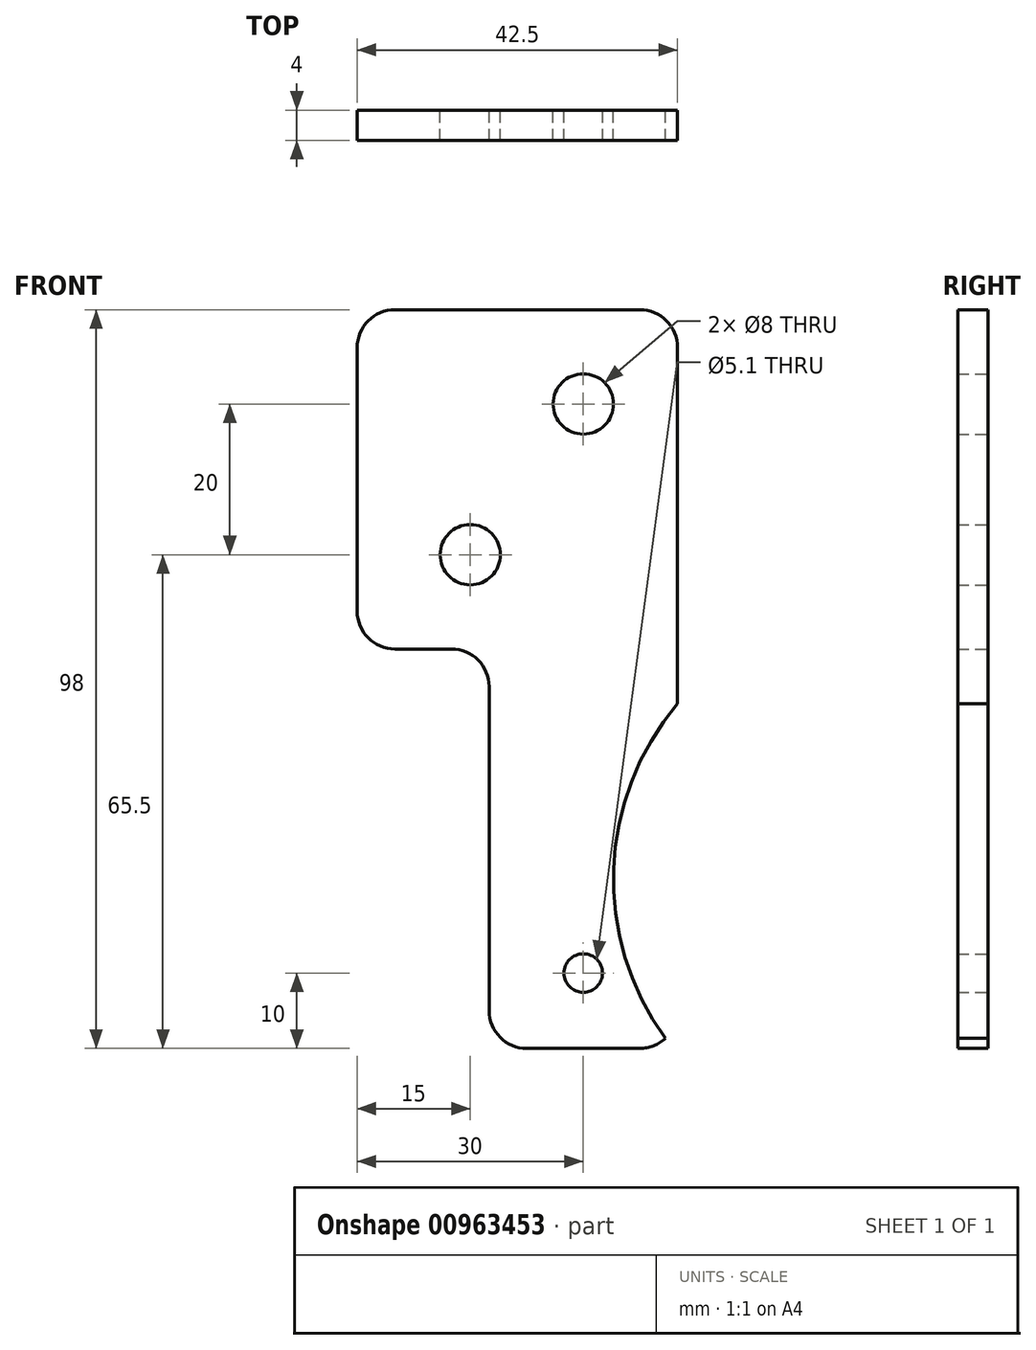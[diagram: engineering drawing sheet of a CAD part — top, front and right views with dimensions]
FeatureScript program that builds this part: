
annotation { "Feature Type Name" : "Feature", "Feature Type Description" : "" }
export const myFeature = defineFeature(function(context is Context, id is Id, definition is map)
    precondition{}
    {
        {
            var Q0;
            Q0=qCreatedBy(makeId("Front.planeOp"),FACE);
            var sketch = newSketch(context, id + "F0", { "sketchPlane" : qUnion([Q0])});
            skLineSegment(sketch, "E0", {"start": v(0, 5) * mm, "end": v(0, 48) * mm});
            skLineSegment(sketch, "E1", {"start": v(-5, 53) * mm, "end": v(-12.5, 53) * mm});
            skLineSegment(sketch, "E2", {"start": v(-17.5, 58) * mm, "end": v(-17.5, 93) * mm});
            skLineSegment(sketch, "E3", {"start": v(-12.5, 98) * mm, "end": v(20, 98) * mm});
            skLineSegment(sketch, "E4", {"start": v(25, 93) * mm, "end": v(25, 45.73) * mm});
            skLineSegment(sketch, "E5", {"start": v(20, 0) * mm, "end": v(5, 0) * mm});
            skPoint(sketch, "E6", {"position": v(12.5, 10) * mm});
            skPoint(sketch, "E7", {"position": v(12.5, 85.5) * mm});
            skPoint(sketch, "E8", {"position": v(-2.5, 65.5) * mm});
            skPoint(sketch, "E9.visualSharp", {"position": v(-17.5, 98) * mm});
            skArc(sketch, "E9.filletArc", {"start": v(-12.5, 98) * mm, "mid": v(-16.04, 96.54) * mm, "end": v(-17.5, 93) * mm});
            skPoint(sketch, "E10.visualSharp", {"position": v(25, 98) * mm});
            skArc(sketch, "E10.filletArc", {"start": v(25, 93) * mm, "mid": v(23.54, 96.54) * mm, "end": v(20, 98) * mm});
            skPoint(sketch, "E11.visualSharp", {"position": v(-17.5, 53) * mm});
            skArc(sketch, "E11.filletArc", {"start": v(-17.5, 58) * mm, "mid": v(-16.04, 54.46) * mm, "end": v(-12.5, 53) * mm});
            skPoint(sketch, "E12.visualSharp", {"position": v(0, 53) * mm});
            skArc(sketch, "E12.filletArc", {"start": v(0, 48) * mm, "mid": v(-1.46, 51.54) * mm, "end": v(-5, 53) * mm});
            skPoint(sketch, "E13.visualSharp", {"position": v(0, 0) * mm});
            skArc(sketch, "E13.filletArc", {"start": v(0, 5) * mm, "mid": v(1.46, 1.46) * mm, "end": v(5, 0) * mm});
            skPoint(sketch, "E14.visualSharp", {"position": v(25, 0) * mm});
            skArc(sketch, "E14.filletArc", {"start": v(20, 0) * mm, "mid": v(21.82, 0.34) * mm, "end": v(23.39, 1.32) * mm});
            skCircle(sketch, "E15", {"center": v(-2.5, 65.5) * mm, "radius": 4 * mm});
            skCircle(sketch, "E16", {"center": v(12.5, 85.5) * mm, "radius": 4 * mm});
            skCircle(sketch, "E17", {"center": v(12.5, 10) * mm, "radius": 2.55 * mm});
            skPoint(sketch, "E18", {"position": v(52.5, 22.5) * mm});
            skArc(sketch, "E19", {"start": v(25, 45.73) * mm, "mid": v(16.52, 23.8) * mm, "end": v(23.39, 1.32) * mm});
            skSolve(sketch);
        }
        {
            var Q0;
            Q0=qSketchRegion(id+"F0",true);
            extrude(context, id + "F1", {"entities" : qUnion([Q0]), "depth" : 4 * mm});
        }
    });
